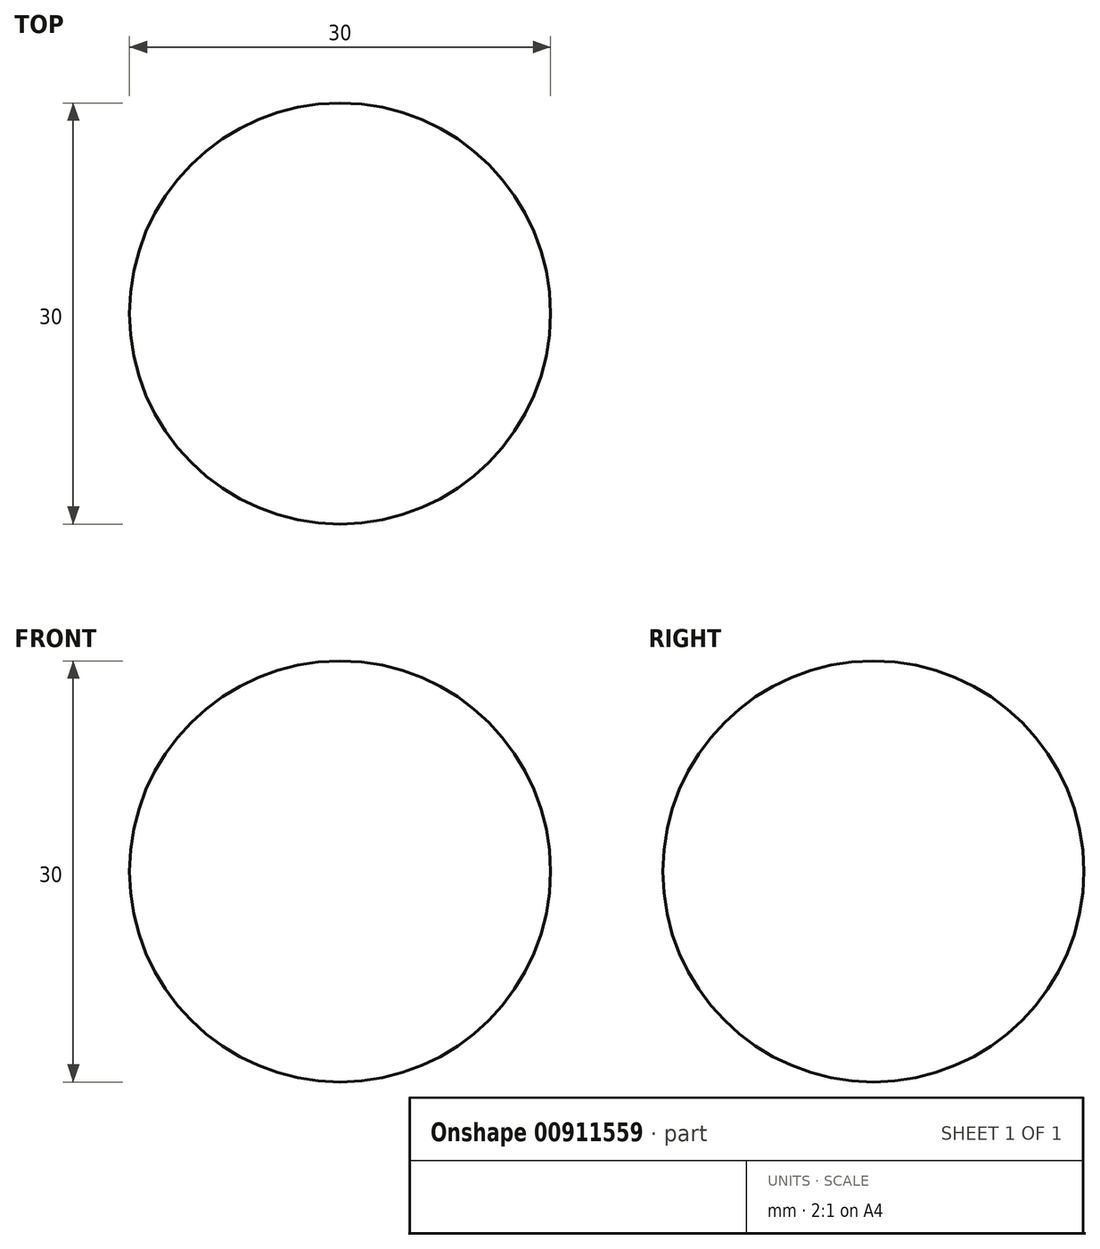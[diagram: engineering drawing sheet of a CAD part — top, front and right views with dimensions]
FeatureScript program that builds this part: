
annotation { "Feature Type Name" : "Feature", "Feature Type Description" : "" }
export const myFeature = defineFeature(function(context is Context, id is Id, definition is map)
    precondition{}
    {
        {
            var Q0;
            Q0=qCreatedBy(makeId("Top.planeOp"),FACE);
            var sketch = newSketch(context, id + "F0", { "sketchPlane" : qUnion([Q0])});
            skPoint(sketch, "E0", {"position": v(0, 15) * mm});
            skPoint(sketch, "E1.orphan", {"position": v(0, 0) * mm});
            skArc(sketch, "E2", {"start": v(0, 0) * mm, "mid": v(15, 15) * mm, "end": v(0, 30) * mm});
            skLineSegment(sketch, "E3", {"start": v(0, 30) * mm, "end": v(0, 0) * mm});
            skSolve(sketch);
        }
        {
            var Q0;
            Q0 = qSketchRegion(id + "F0", true);
            var Q1;
            Q1=sQuery(id+"F0.wireOp",EDGE,"E3");
            revolve(context, id + "F1", {"surfaceOperationType" : NewSurfaceOperationType.NEW, "entities" : qUnion([Q0]), "axis" : qUnion([Q1]), "revolveType" : RevolveType.FULL});
        }
    });
